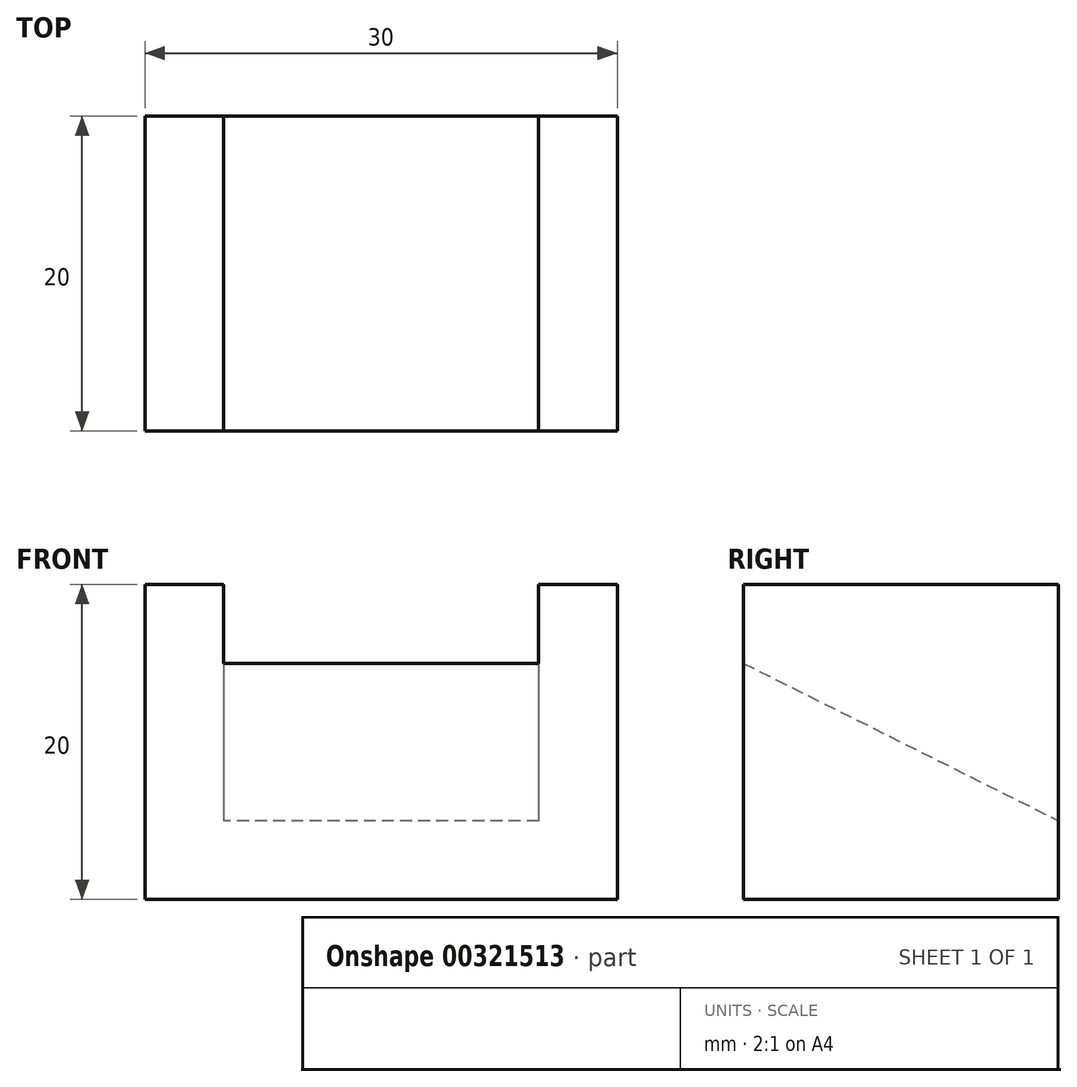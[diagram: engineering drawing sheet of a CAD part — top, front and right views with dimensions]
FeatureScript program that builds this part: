
annotation { "Feature Type Name" : "Feature", "Feature Type Description" : "" }
export const myFeature = defineFeature(function(context is Context, id is Id, definition is map)
    precondition{}
    {
        {
            var Q0;
            Q0=qCreatedBy(makeId("Front.planeOp"),FACE);
            var sketch = newSketch(context, id + "F0", { "sketchPlane" : qUnion([Q0])});
            skLineSegment(sketch, "E0.bottom", {"start": v(-15, 20) * mm, "end": v(15, 20) * mm});
            skLineSegment(sketch, "E0.top", {"start": v(-15, 0) * mm, "end": v(15, 0) * mm});
            skLineSegment(sketch, "E0.left", {"start": v(-15, 20) * mm, "end": v(-15, 0) * mm});
            skLineSegment(sketch, "E0.right", {"start": v(15, 20) * mm, "end": v(15, 0) * mm});
            skSolve(sketch);
        }
        {
            var Q0;
            Q0=makeQuery(id+"F0.imprint","IMPRINT",FACE,{"disambiguationData":[TD([[makeQuery(id+"F0.imprint","IMPRINT",EDGE,{"derivedFrom":sQuery(id+"F0.wireOp",EDGE,"E0.bottom")}),-1.0]])]});
            extrude(context, id + "F1", {"entities" : qUnion([Q0]), "depth" : 20 * mm});
        }
        {
            var Q0;
            Q0=makeQuery(id+"F1.opExtrude","SWEPT_FACE",FACE,{"disambiguationData":[OSD([sQuery(id+"F0.wireOp",EDGE,"E0.left")])]});
            var sketch = newSketch(context, id + "F2", { "sketchPlane" : qUnion([Q0])});
            skLineSegment(sketch, "E1", {"start": v(20, 15) * mm, "end": v(0, 5) * mm});
            skLineSegment(sketch, "E2", {"start": v(0, 5) * mm, "end": v(20, 5) * mm});
            skLineSegment(sketch, "E3", {"start": v(20, 5) * mm, "end": v(20, 15) * mm});
            skSolve(sketch);
        }
        {
            var Q0;
            {var subQ0=sQuery(id+"F2.wireOp",EDGE,"E1");Q0=makeQuery(id+"F2.imprint","IMPRINT",FACE,{"disambiguationData":[TD([[makeQuery(id+"F2.imprint","IMPRINT",EDGE,{"derivedFrom":subQ0}),-1.0]])]});}
            extrude(context, id + "F3", {"entities" : qUnion([Q0]), "operationType" : NewBodyOperationType.REMOVE, "oppositeDirection" : true, "depth" : 25 * mm, "hasSecondDirection" : true, "secondDirectionOppositeDirection" : true, "secondDirectionDepth" : 5 * mm});
        }
    });
